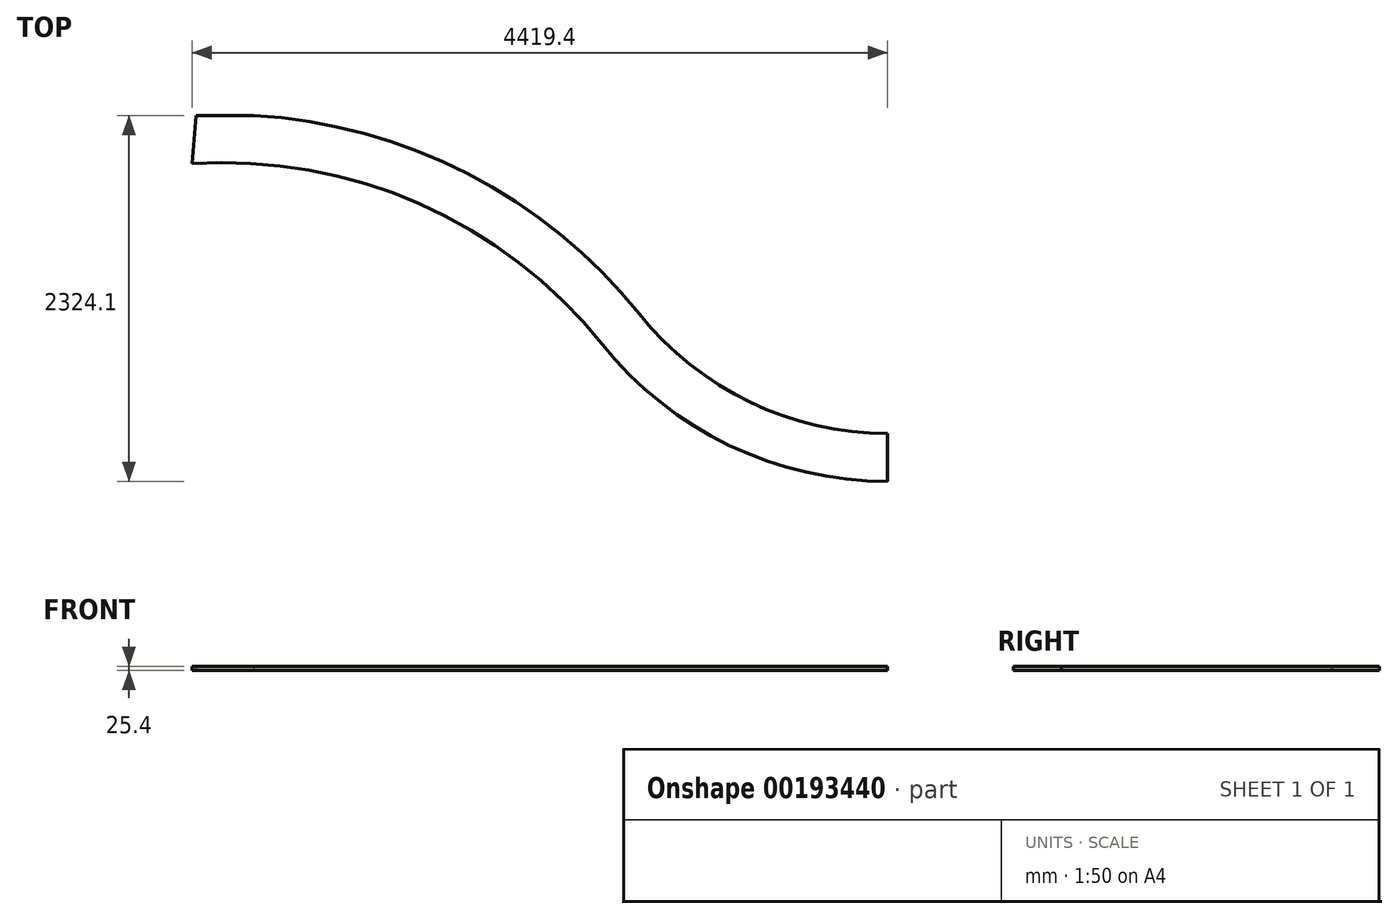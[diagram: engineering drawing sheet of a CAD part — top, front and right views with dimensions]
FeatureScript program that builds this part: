
annotation { "Feature Type Name" : "Feature", "Feature Type Description" : "" }
export const myFeature = defineFeature(function(context is Context, id is Id, definition is map)
    precondition{}
    {
        {
            var Q0;
            Q0=qCreatedBy(makeId("Top.planeOp"),FACE);
            var sketch = newSketch(context, id + "F0", { "sketchPlane" : qUnion([Q0])});
            skLineSegment(sketch, "E0", {"start": v(-2322.3, 99.74) * mm, "end": v(363.78, 99.74) * mm});
            skLineSegment(sketch, "E1", {"start": v(2078.28, -1614.76) * mm, "end": v(2078.28, -2224.36) * mm});
            skArc(sketch, "E2", {"start": v(2078.28, -1614.76) * mm, "mid": v(865.95, -1112.6) * mm, "end": v(363.78, 99.74) * mm});
            skArc(sketch, "E3.0", {"start": v(2078.28, -1919.56) * mm, "mid": v(1203.8, -1720.4) * mm, "end": v(501.84, -1162.16) * mm});
            skArc(sketch, "E4.0", {"start": v(2078.28, -2224.36) * mm, "mid": v(1071.81, -1995.13) * mm, "end": v(263.88, -1352.64) * mm});
            skLineSegment(sketch, "E5", {"start": v(-2322.3, 99.74) * mm, "end": v(-2341.12, -206.78) * mm});
            skPoint(sketch, "E6", {"position": v(-2322.3, 99.74) * mm});
            skArc(sketch, "E7", {"start": v(501.84, -1162.16) * mm, "mid": v(-757.31, -188.98) * mm, "end": v(-2322.3, 99.74) * mm});
            skArc(sketch, "E8.0", {"start": v(263.88, -1352.64) * mm, "mid": v(-898, -460.02) * mm, "end": v(-2341.12, -206.78) * mm});
            skPoint(sketch, "E9.orphan", {"position": v(-2399.79, -1162.16) * mm});
            skLineSegment(sketch, "E10", {"start": v(2078.28, 99.74) * mm, "end": v(0, -1978.55) * mm});
            skLineSegment(sketch, "E11", {"start": v(-2341.12, -206.78) * mm, "end": v(-2322.3, 99.74) * mm});
            skLineSegment(sketch, "E12", {"start": v(2078.28, -1614.76) * mm, "end": v(2052.9, -1614.09) * mm});
            skLineSegment(sketch, "E13.0", {"start": v(2052.88, -1614.09) * mm, "end": v(2052.88, -2223.26) * mm});
            skLineSegment(sketch, "E14", {"start": v(-2339.55, -181.22) * mm, "end": v(-2322.3, 99.74) * mm});
            skLineSegment(sketch, "E15", {"start": v(-2341.12, -206.78) * mm, "end": v(-2314.2, 100.17) * mm});
            skSolve(sketch);
        }
        {
            var Q0;
            {var subQ9=sQuery(id+"F0.wireOp",EDGE,"E8.0");Q0=makeQuery(id+"F0.imprint","IMPRINT",FACE,{"disambiguationData":[TD([[makeQuery(id+"F0.imprint","IMPRINT",EDGE,{"derivedFrom":subQ9}),-1.0]])]});}
            extrude(context, id + "F1", {"entities" : qUnion([Q0]), "depth" : 25.4 * mm});
        }
        {
            var Q0;
            {var subQ0=sQuery(id+"F0.wireOp",EDGE,"E4.0");var subQ1=sQuery(id+"F0.wireOp",EDGE,"E1");var subQ2=makeQuery(id+"F0.imprint","INTERSECT",VERTEX,{"derivedFrom":[subQ1,subQ0]});Q0=makeQuery(id+"F0.imprint","IMPRINT",FACE,{"disambiguationData":[TD([[makeQuery(id+"F0.imprint","IMPRINT",EDGE,{"disambiguationData":[TD([[subQ2,1.0]])],"derivedFrom":subQ1}),-1.0]])]});}
            extrude(context, id + "F2", {"entities" : qUnion([Q0]), "operationType" : NewBodyOperationType.ADD, "depth" : 25.4 * mm});
        }
    });
